# Revit family: Domotics-DomesticRanges-GEWISS-CHORUS_CONTAINER_INSTRUMENT_BLACK
name_source: partatom
category: Apparecchi elettrici
revit_build: Autodesk Revit 2016 (Build: 20161004_0715(x64)
units: mm (PartAtom-declared; Revit-internal decimal feet)

## family parameters
Basato su piano di lavoro = No
Condiviso = No
Mantenere orientamento annotazione = No
Punto di calcolo locali = No
Quota connettore circolare = Usa diametro
Sempre verticale = Sì
Taglio con vuoti quando caricato = No
Tipo di parte = Normale

## types (2) — shared parameters
Catalogue = DOMOTICS
Catalogue Range = CHORUS - DOMESTIC RANGE
Colour = Black
Electrocod = 0122
Glow Wire Test = 650 °C
Glow wire test: = 650 °C
IDF = 44767252-c965-40fb-be1e-8c35ed1d6c89
IDT = 285ffd39-813f-4bf7-a378-0da872310e95
Immagine tipo = GW16864.jpg
Larghezza = 181 mm  [stored 0.593832 ft]
Material = Rectangular
Materiale_ = GEWISS NERO
Produttore = GEWISS S.p.A.
SEO = Panel
Standard = EN 60670-1
Standard; = EN 60670-1
Suitable for plates = ONE
Technical sheet = https://www.gewiss.com
Thermo-pressure with ball = 70
Torque screws tightening = 0,8NM
URL = https://www.gewiss.com
Version file RFA = 18.0

## per-type parameters (varying)
| type | Description: | Descrizione | EAN code | Modello | Outer dim. LxHxD (mm) | Support |
| GW16866 - Table plate 6P Black | 6 gang | TABLE AND WALL PLATE, 6-GANG, BLACK | 8011564279445 | GW16866 | 181x90x69 | GW16806 |
| GW16864 - Table plate 4P Black | 4 gang | TABLE AND WALL PLATE, 4-GANG, BLACK | 8011564278103 | GW16864 | 140x90x69 | GW16804 |

note: source unit labels omitted for Thermo-pressure with ball — the stored unit's dimension contradicts the parameter name (converter mislabeling)

note: [stored X ft] marks values corroborated as IEEE doubles in the binary element streams (Revit-internal decimal feet)
